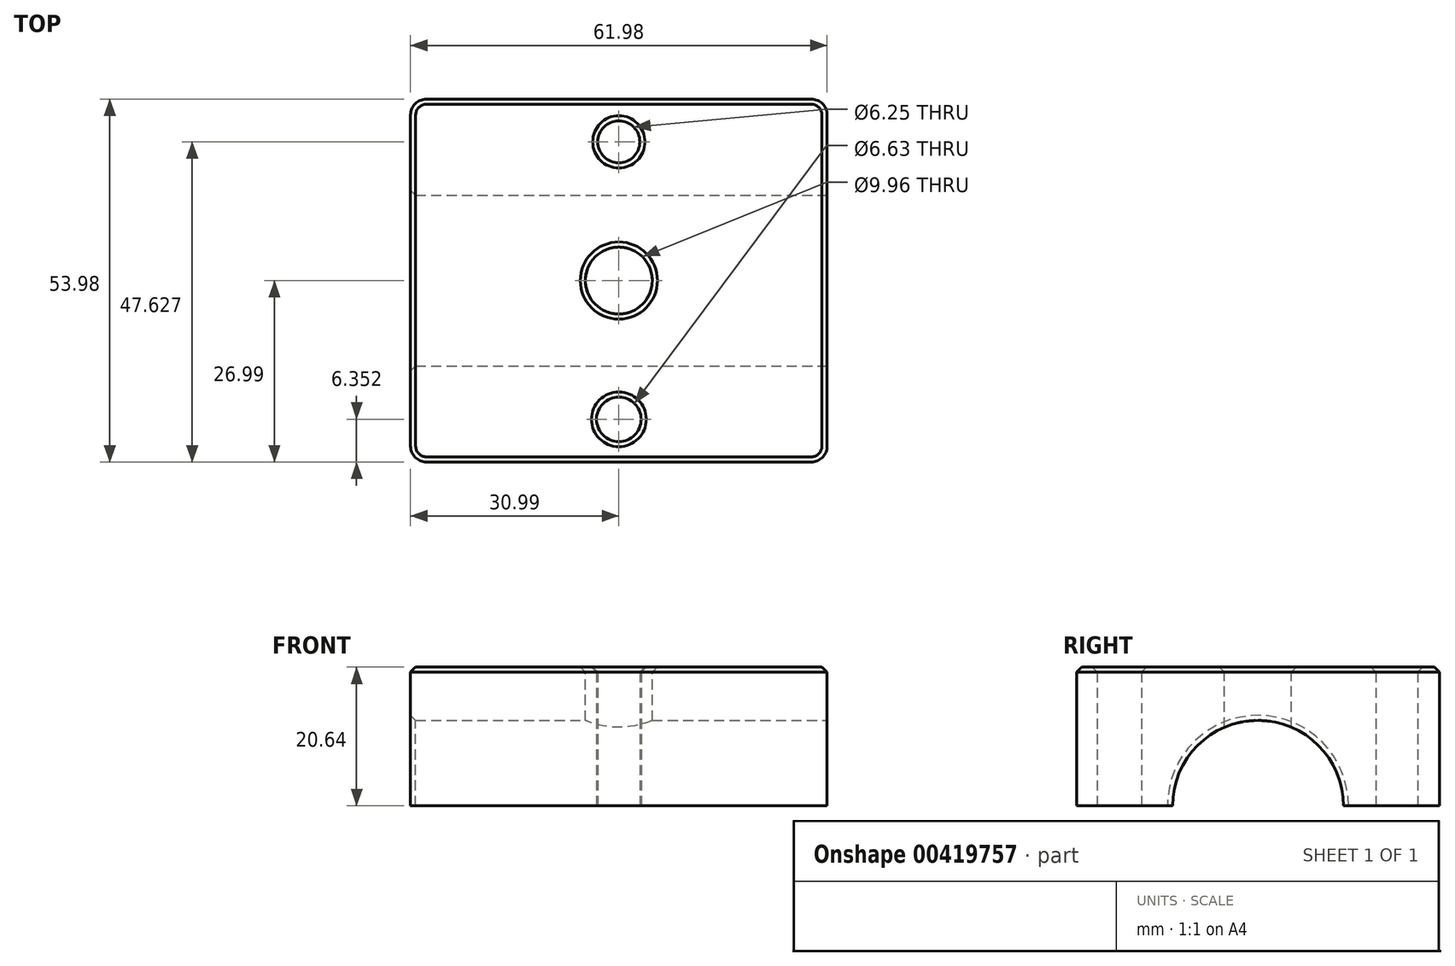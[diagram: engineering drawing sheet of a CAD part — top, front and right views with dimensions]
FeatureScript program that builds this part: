
annotation { "Feature Type Name" : "Feature", "Feature Type Description" : "" }
export const myFeature = defineFeature(function(context is Context, id is Id, definition is map)
    precondition{}
    {
        {
            var Q0;
            Q0=qCreatedBy(makeId("Top.planeOp"),FACE);
            var sketch = newSketch(context, id + "F0", { "sketchPlane" : qUnion([Q0])});
            skLineSegment(sketch, "E0.bottom", {"start": v(30.99, -26.99) * mm, "end": v(-30.99, -26.99) * mm});
            skLineSegment(sketch, "E0.top", {"start": v(30.99, 26.99) * mm, "end": v(-30.99, 26.99) * mm});
            skLineSegment(sketch, "E0.left", {"start": v(30.99, -26.99) * mm, "end": v(30.99, 26.99) * mm});
            skLineSegment(sketch, "E0.right", {"start": v(-30.99, -26.99) * mm, "end": v(-30.99, 26.99) * mm});
            skPoint(sketch, "E0.middle", {"position": v(0, 0) * mm});
            skLineSegment(sketch, "E1", {"start": v(0, 81.83) * mm, "end": v(0, -89.25) * mm, "construction": true});
            skLineSegment(sketch, "E2", {"start": v(-95.47, 0) * mm, "end": v(125.13, 0) * mm, "construction": true});
            skLineSegment(sketch, "E3", {"start": v(-25.4, 38.93) * mm, "end": v(-25.4, -60.9) * mm, "construction": true});
            skLineSegment(sketch, "E4", {"start": v(25.4, 39.99) * mm, "end": v(25.4, -57.2) * mm, "construction": true});
            skPoint(sketch, "E5", {"position": v(-25.4, 0) * mm});
            skPoint(sketch, "E6", {"position": v(25.4, 0) * mm});
            skPoint(sketch, "E6.positionSnap0", {"position": v(30.99, 0) * mm});
            skSolve(sketch);
        }
        {
            var Q0;
            Q0=makeQuery(id+"F0.imprint","IMPRINT",FACE,{"disambiguationData":[TD([[makeQuery(id+"F0.imprint","IMPRINT",EDGE,{"derivedFrom":sQuery(id+"F0.wireOp",EDGE,"E0.bottom")}),-1.0]])]});
            extrude(context, id + "F1", {"entities" : qUnion([Q0]), "depth" : 41.27 * mm});
        }
        {
            var Q0;
            Q0=qCreatedBy(makeId("Top.planeOp"),FACE);
            var sketch = newSketch(context, id + "F2", { "sketchPlane" : qUnion([Q0])});
            skLineSegment(sketch, "E7", {"start": v(0, 51.37) * mm, "end": v(0, -56.11) * mm, "construction": true});
            skLineSegment(sketch, "E8", {"start": v(-42.71, 20.64) * mm, "end": v(42.71, 20.64) * mm, "construction": true});
            skLineSegment(sketch, "E9", {"start": v(-41.04, -20.64) * mm, "end": v(46.62, -20.64) * mm, "construction": true});
            skPoint(sketch, "E10", {"position": v(0, -20.64) * mm});
            skCircle(sketch, "E11", {"center": v(0, 20.64) * mm, "radius": 3.12 * mm});
            skCircle(sketch, "E12", {"center": v(0, -20.64) * mm, "radius": 3.32 * mm});
            skSolve(sketch);
        }
        {
            var Q0;
            Q0=makeQuery(id+"F2.imprint","IMPRINT",FACE,{"disambiguationData":[TD([[makeQuery(id+"F2.imprint","IMPRINT",EDGE,{"derivedFrom":sQuery(id+"F2.wireOp",EDGE,"E12")}),1.0]])]});
            var Q1;
            Q1=makeQuery(id+"F2.imprint","IMPRINT",FACE,{"disambiguationData":[TD([[makeQuery(id+"F2.imprint","IMPRINT",EDGE,{"derivedFrom":sQuery(id+"F2.wireOp",EDGE,"E11")}),1.0]])]});
            extrude(context, id + "F3", {"entities" : qUnion([Q0, Q1]), "operationType" : NewBodyOperationType.REMOVE, "depth" : 41.27 * mm});
        }
        {
            var Q0;
            Q0=makeQuery(id+"F1.opExtrude","SWEPT_FACE",FACE,{"disambiguationData":[OSD([sQuery(id+"F0.wireOp",EDGE,"E0.left")])]});
            var sketch = newSketch(context, id + "F4", { "sketchPlane" : qUnion([Q0])});
            skLineSegment(sketch, "E13", {"start": v(26.99, 41.28) * mm, "end": v(-26.99, 0) * mm});
            skLineSegment(sketch, "E14", {"start": v(-26.99, 41.28) * mm, "end": v(26.99, 0) * mm});
            skCircle(sketch, "E15", {"center": v(0, 20.64) * mm, "radius": 12.7 * mm});
            skSolve(sketch);
        }
        {
            var Q0;
            Q0 = qSketchRegion(id + "F4", true);
            extrude(context, id + "F5", {"entities" : qUnion([Q0]), "operationType" : NewBodyOperationType.REMOVE, "endBound" : BoundingType.THROUGH_ALL, "oppositeDirection" : true, "depth" : 25.4 * mm});
        }
        {
            var Q0;
            Q0=makeQuery(id+"F1.opExtrude","SWEPT_FACE",FACE,{"disambiguationData":[OSD([sQuery(id+"F0.wireOp",EDGE,"E0.bottom")])]});
            var sketch = newSketch(context, id + "F6", { "sketchPlane" : qUnion([Q0])});
            skLineSegment(sketch, "E16", {"start": v(-16.5, 49.26) * mm, "end": v(-16.5, -12.65) * mm});
            skLineSegment(sketch, "E17", {"start": v(-42.4, 20.64) * mm, "end": v(53.22, 20.64) * mm});
            skPoint(sketch, "E17.startSnap0", {"position": v(-30.99, 20.64) * mm});
            skPoint(sketch, "E18", {"position": v(-16.5, 20.64) * mm});
            skCircle(sketch, "E19", {"center": v(-16.5, 20.64) * mm, "radius": 3.18 * mm});
            skSolve(sketch);
        }
        {
            var Q0;
            {var subQ0=sQuery(id+"F6.wireOp",EDGE,"E19");var subQ1=sQuery(id+"F6.wireOp",EDGE,"E16");var subQ2=makeQuery(id+"F6.imprint","INTERSECT",VERTEX,{"disambiguationData":[OD(0.0)],"derivedFrom":[subQ1,subQ0]});Q0=makeQuery(id+"F6.imprint","IMPRINT",FACE,{"disambiguationData":[TD([[makeQuery(id+"F6.imprint","IMPRINT",EDGE,{"disambiguationData":[TD([[subQ2,-1.0]])],"derivedFrom":subQ1}),-1.0]])]});}
            var Q1;
            {var subQ0=sQuery(id+"F6.wireOp",EDGE,"E19");var subQ1=sQuery(id+"F6.wireOp",EDGE,"E16");var subQ2=makeQuery(id+"F6.imprint","INTERSECT",VERTEX,{"disambiguationData":[OD(0.0)],"derivedFrom":[subQ1,subQ0]});Q1=makeQuery(id+"F6.imprint","IMPRINT",FACE,{"disambiguationData":[TD([[makeQuery(id+"F6.imprint","IMPRINT",EDGE,{"disambiguationData":[TD([[subQ2,-1.0]])],"derivedFrom":subQ1}),1.0]])]});}
            var Q2;
            {var subQ0=sQuery(id+"F6.wireOp",EDGE,"E17");var subQ1=sQuery(id+"F6.wireOp",EDGE,"E16");var subQ2=makeQuery(id+"F6.imprint","INTERSECT",VERTEX,{"derivedFrom":[subQ1,subQ0]});Q2=makeQuery(id+"F6.imprint","IMPRINT",FACE,{"disambiguationData":[TD([[makeQuery(id+"F6.imprint","IMPRINT",EDGE,{"disambiguationData":[TD([[subQ2,-1.0]])],"derivedFrom":subQ1}),1.0]])]});}
            var Q3;
            {var subQ0=sQuery(id+"F6.wireOp",EDGE,"E17");var subQ1=sQuery(id+"F6.wireOp",EDGE,"E16");var subQ2=makeQuery(id+"F6.imprint","INTERSECT",VERTEX,{"derivedFrom":[subQ1,subQ0]});Q3=makeQuery(id+"F6.imprint","IMPRINT",FACE,{"disambiguationData":[TD([[makeQuery(id+"F6.imprint","IMPRINT",EDGE,{"disambiguationData":[TD([[subQ2,-1.0]])],"derivedFrom":subQ1}),-1.0]])]});}
            extrude(context, id + "F7", {"entities" : qUnion([Q0, Q1, Q2, Q3]), "operationType" : NewBodyOperationType.REMOVE, "endBound" : BoundingType.THROUGH_ALL, "oppositeDirection" : true, "depth" : 25.4 * mm});
        }
        {
            var Q0;
            Q0=makeQuery(id+"F1.opExtrude","CAP_FACE",FACE,{"disambiguationData":[OSD([sQuery(id+"F0.wireOp",EDGE,"E0.bottom"),sQuery(id+"F0.wireOp",EDGE,"E0.top"),sQuery(id+"F0.wireOp",EDGE,"E0.left"),sQuery(id+"F0.wireOp",EDGE,"E0.right")])],"isStart":false});
            var sketch = newSketch(context, id + "F8", { "sketchPlane" : qUnion([Q0])});
            skCircle(sketch, "E20", {"center": v(0, 0) * mm, "radius": 4.98 * mm});
            skSolve(sketch);
        }
        {
            var Q0;
            Q0 = qSketchRegion(id + "F8", true);
            extrude(context, id + "F9", {"entities" : qUnion([Q0]), "operationType" : NewBodyOperationType.REMOVE, "endBound" : BoundingType.THROUGH_ALL, "oppositeDirection" : true, "depth" : 25.4 * mm});
        }
        {
            var Q0;
            Q0=makeQuery(id+"F1.opExtrude","SWEPT_EDGE",EDGE,{"disambiguationData":[OSD([sQuery(id+"F0.wireOp",EDGE,"E0.bottom"),sQuery(id+"F0.wireOp",EDGE,"E0.left")])]});
            var Q1;
            Q1=makeQuery(id+"F1.opExtrude","SWEPT_EDGE",EDGE,{"disambiguationData":[OSD([sQuery(id+"F0.wireOp",EDGE,"E0.top"),sQuery(id+"F0.wireOp",EDGE,"E0.left")])]});
            var Q2;
            Q2=makeQuery(id+"F1.opExtrude","SWEPT_EDGE",EDGE,{"disambiguationData":[OSD([sQuery(id+"F0.wireOp",EDGE,"E0.bottom"),sQuery(id+"F0.wireOp",EDGE,"E0.right")])]});
            var Q3;
            Q3=makeQuery(id+"F1.opExtrude","SWEPT_EDGE",EDGE,{"disambiguationData":[OSD([sQuery(id+"F0.wireOp",EDGE,"E0.top"),sQuery(id+"F0.wireOp",EDGE,"E0.right")])]});
            var Q4;
            Q4=makeQuery(id+"F1.opExtrude","CAP_EDGE",EDGE,{"disambiguationData":[OSD([sQuery(id+"F0.wireOp",EDGE,"E0.bottom")])],"isStart":true});
            var Q5;
            Q5=makeQuery(id+"F1.opExtrude","CAP_EDGE",EDGE,{"disambiguationData":[OSD([sQuery(id+"F0.wireOp",EDGE,"E0.left")])],"isStart":true});
            var Q6;
            Q6=makeQuery(id+"F1.opExtrude","CAP_EDGE",EDGE,{"disambiguationData":[OSD([sQuery(id+"F0.wireOp",EDGE,"E0.right")])],"isStart":true});
            var Q7;
            Q7=makeQuery(id+"F1.opExtrude","CAP_EDGE",EDGE,{"disambiguationData":[OSD([sQuery(id+"F0.wireOp",EDGE,"E0.top")])],"isStart":true});
            fillet(context, id + "F10", {"entities" : qUnion([Q0, Q1, Q2, Q3, Q4, Q5, Q6, Q7]), "radius" : 2.36 * mm, "tangentPropagation" : true, "allowEdgeOverflow" : false});
        }
        {
            var Q0;
            Q0=makeQuery(id+"F5.boolean.opBoolean","COPY",EDGE,{"derivedFrom":makeQuery(id+"F5.opExtrude","CAP_EDGE",EDGE,{"disambiguationData":[OSD([sQuery(id+"F4.wireOp",EDGE,"E15")])],"isStart":true})});
            var Q1;
            Q1=makeQuery(id+"F5.boolean.opBoolean","INTERSECT",EDGE,{"derivedFrom":[makeQuery(id+"F1.opExtrude","SWEPT_FACE",FACE,{"disambiguationData":[OSD([sQuery(id+"F0.wireOp",EDGE,"E0.right")])]}),makeQuery(id+"F5.opExtrude","SWEPT_FACE",FACE,{"disambiguationData":[OSD([sQuery(id+"F4.wireOp",EDGE,"E15")])]})]});
            var Q2;
            Q2=makeQuery(id+"F1.opExtrude","CAP_FACE",FACE,{"disambiguationData":[OSD([sQuery(id+"F0.wireOp",EDGE,"E0.bottom"),sQuery(id+"F0.wireOp",EDGE,"E0.top"),sQuery(id+"F0.wireOp",EDGE,"E0.left"),sQuery(id+"F0.wireOp",EDGE,"E0.right")])],"isStart":false});
            var Q3;
            Q3=makeQuery(id+"F7.boolean.opBoolean","COPY",EDGE,{"derivedFrom":makeQuery(id+"F7.opExtrude","CAP_EDGE",EDGE,{"disambiguationData":[OSD([sQuery(id+"F6.wireOp",EDGE,"E19")])],"isStart":true})});
            var Q4;
            Q4=makeQuery(id+"F3.boolean.opBoolean","COPY",EDGE,{"derivedFrom":makeQuery(id+"F3.opExtrude","CAP_EDGE",EDGE,{"disambiguationData":[OSD([sQuery(id+"F2.wireOp",EDGE,"E12")])],"isStart":true})});
            var Q5;
            Q5=makeQuery(id+"F3.boolean.opBoolean","COPY",EDGE,{"derivedFrom":makeQuery(id+"F3.opExtrude","CAP_EDGE",EDGE,{"disambiguationData":[OSD([sQuery(id+"F2.wireOp",EDGE,"E11")])],"isStart":true})});
            var Q6;
            Q6=makeQuery(id+"F7.boolean.opBoolean","INTERSECT",EDGE,{"derivedFrom":[makeQuery(id+"F1.opExtrude","SWEPT_FACE",FACE,{"disambiguationData":[OSD([sQuery(id+"F0.wireOp",EDGE,"E0.top")])]}),makeQuery(id+"F7.opExtrude","SWEPT_FACE",FACE,{"disambiguationData":[OSD([sQuery(id+"F6.wireOp",EDGE,"E19")])]})]});
            chamfer(context, id + "F11", {"entities" : qUnion([Q0, Q1, Q2, Q3, Q4, Q5, Q6]), "width" : 0.76 * mm, "tangentPropagation" : true});
        }
    });
